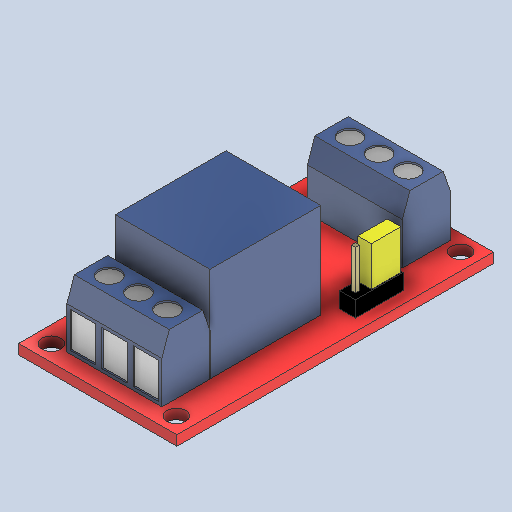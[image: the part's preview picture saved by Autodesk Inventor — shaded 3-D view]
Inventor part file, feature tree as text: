
AUTODESK INVENTOR PART (.ipt)
format: ipt  version: 2024 (Build 280153000, 153)  size: 559,616 bytes
history: native  units: in
note: dims shown in document units (in); Inventor stores cm internally (conversion verified against a paired STEP export)
features: sketch x10, extrude x9, projected_geometry x4, chamfer x2, fillet x1
ambient origin geometry x8: Origin, YZ Plane, XZ Plane, XY Plane, X Axis, Y Axis, Z Axis, Center Point
bodies: Solid1 (feature_tree)
feature tree (26):
  extrude  "Extrusion1"  Depth=2.0in
  extrude  "Extrusion2"  Depth=0.045in
  chamfer  "Chamfer1"  Distance=0.063in
  chamfer  "Chamfer2"  Distance=0.3in
  extrude  "Extrusion3"  Depth=0.305in
  extrude  "Extrusion4"  Depth=0.6in
  extrude  "Extrusion5"  Depth=0.4in TaperAngle=0.0deg
  extrude  "Extrusion6"  Depth=0.02in TaperAngle=45.0deg
  extrude  "Extrusion7"  Depth=0.02in TaperAngle=45.0deg
  extrude  "Extrusion8"  Depth=0.02in
  extrude  "Extrusion9"  Depth=0.02in
  fillet  "Fillet1"  Radius=0.135in
  sketch  "Sketch12"  dims[d19=0.305in d20=0.3in d21=0.305in d22=0.6in d23=0.4in d24=0.0in d25=0.047in d26=0.135in d27=45.0deg d28=0.047in d29=0.135in d30=45.0deg d31=0.135in d32=0.135in d33=0.135in d34=0.135in d35=0.135in d36=0.135in d37=0.01in d38=0.0in d39=0.2in d40=0.2in d41=0.02in d42=0.02in d43=0.02in d44=0.02in d45=0.02in d46=0.01in d47=0.0in d48=0.2in d49=0.2in d50=0.02in d51=0.02in d52=0.02in d53=0.02in d54=0.02in d55=0.01in d56=0.0in d57=0.299in d58=0.7in d59=0.299in d60=0.74in d61=0.6in d62=0.0in d63=0.1in d64=0.0in d65=0.3in d66=0.1in d67=0.2in d68=0.25in d69=0.0in d70=0.08in d71=0.08in d72=0.08in d73=0.08in d74=0.08in d75=0.08in d76=0.05in d77=0.05in d78=0.05in d79=0.08in d80=0.08in d81=0.08in d82=0.08in d83=0.0in d84=0.02in]
  sketch  "Sketch1"  dims[d0=1.0in d1=2.0in]
  sketch  "Sketch3"  dims[d2=0.045in d3=0.045in]
  sketch  "Sketch4"  dims[d4=0.12in d5=0.063in d6=0.0in]
  sketch  "Sketch5"  dims[d13=0.305in]
  sketch  "Sketch6"  dims[d14=0.07in]
  sketch  "Sketch7"  dims[d15=0.105in]
  sketch  "Sketch8"  dims[d16=0.305in]
  sketch  "Sketch10"  dims[d17=0.3in]
  projected_geometry  "Projected Loop1"
  sketch  "Sketch11"  dims[d18=0.6in]
  projected_geometry  "Projected Loop2"
  projected_geometry  "Projected Loop3"
  projected_geometry  "Projected Loop4"
